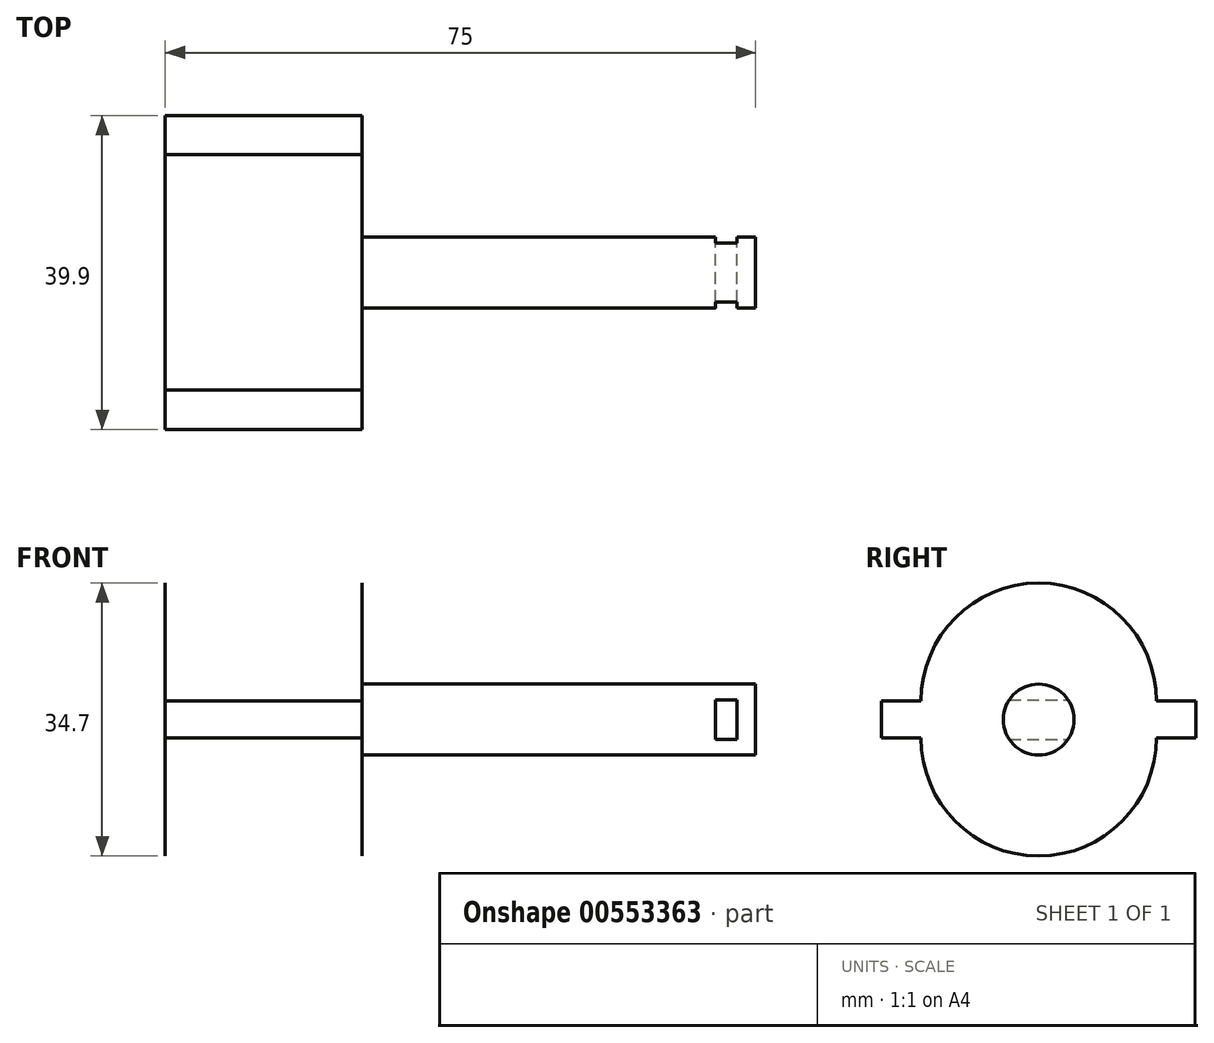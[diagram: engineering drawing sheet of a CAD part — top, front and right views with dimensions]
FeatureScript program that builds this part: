
annotation { "Feature Type Name" : "Feature", "Feature Type Description" : "" }
export const myFeature = defineFeature(function(context is Context, id is Id, definition is map)
    precondition{}
    {
        {
            var Q0;
            Q0=qCreatedBy(makeId("Right.planeOp"),FACE);
            var sketch = newSketch(context, id + "F0", { "sketchPlane" : qUnion([Q0])});
            skLineSegment(sketch, "E0.bottom", {"start": v(14.95, 17.35) * mm, "end": v(-14.95, 17.35) * mm});
            skLineSegment(sketch, "E0.top", {"start": v(14.95, -17.35) * mm, "end": v(-14.95, -17.35) * mm});
            skLineSegment(sketch, "E0.left", {"start": v(14.95, 17.35) * mm, "end": v(14.95, -17.35) * mm});
            skLineSegment(sketch, "E0.right", {"start": v(-14.95, 17.35) * mm, "end": v(-14.95, -17.35) * mm});
            skPoint(sketch, "E0.middle", {"position": v(0, 0) * mm});
            skSolve(sketch);
        }
        {
            var Q0;
            Q0=makeQuery(id+"F0.imprint","IMPRINT",FACE,{"disambiguationData":[TD([[makeQuery(id+"F0.imprint","IMPRINT",EDGE,{"derivedFrom":sQuery(id+"F0.wireOp",EDGE,"E0.bottom")}),1.0]])]});
            extrude(context, id + "F1", {"entities" : qUnion([Q0]), "oppositeDirection" : true, "depth" : 25 * mm, "offsetDistance" : 25 * mm});
        }
        {
            var Q0;
            Q0=qCreatedBy(makeId("Right.planeOp"),FACE);
            var sketch = newSketch(context, id + "F2", { "sketchPlane" : qUnion([Q0])});
            skCircle(sketch, "E1", {"center": v(0, 0) * mm, "radius": 4.5 * mm});
            skSolve(sketch);
        }
        {
            var Q0;
            Q0=makeQuery(id+"F2.imprint","IMPRINT",FACE,{"disambiguationData":[TD([[makeQuery(id+"F2.imprint","IMPRINT",EDGE,{"derivedFrom":sQuery(id+"F2.wireOp",EDGE,"E1")}),1.0]])]});
            extrude(context, id + "F3", {"entities" : qUnion([Q0]), "operationType" : NewBodyOperationType.ADD, "depth" : 50 * mm, "offsetDistance" : 25 * mm});
        }
        {
            var Q0;
            Q0=makeQuery(id+"F1.opExtrude","SWEPT_EDGE",EDGE,{"disambiguationData":[OSD([sQuery(id+"F0.wireOp",EDGE,"E0.bottom"),sQuery(id+"F0.wireOp",EDGE,"E0.right")])]});
            var Q1;
            Q1=makeQuery(id+"F1.opExtrude","SWEPT_EDGE",EDGE,{"disambiguationData":[OSD([sQuery(id+"F0.wireOp",EDGE,"E0.top"),sQuery(id+"F0.wireOp",EDGE,"E0.left")])]});
            var Q2;
            Q2=makeQuery(id+"F1.opExtrude","SWEPT_EDGE",EDGE,{"disambiguationData":[OSD([sQuery(id+"F0.wireOp",EDGE,"E0.bottom"),sQuery(id+"F0.wireOp",EDGE,"E0.left")])]});
            var Q3;
            Q3=makeQuery(id+"F1.opExtrude","SWEPT_EDGE",EDGE,{"disambiguationData":[OSD([sQuery(id+"F0.wireOp",EDGE,"E0.top"),sQuery(id+"F0.wireOp",EDGE,"E0.right")])]});
            fillet(context, id + "F4", {"entities" : qUnion([Q0, Q1, Q2, Q3]), "radius" : 15 * mm, "tangentPropagation" : true, "allowEdgeOverflow" : false});
        }
        {
            var Q0;
            Q0=makeQuery(id+"F1.opExtrude","SWEPT_FACE",FACE,{"disambiguationData":[OSD([sQuery(id+"F0.wireOp",EDGE,"E0.left")])]});
            extrude(context, id + "F5", {"entities" : qUnion([Q0]), "operationType" : NewBodyOperationType.ADD, "depth" : 5 * mm, "offsetDistance" : 25 * mm});
        }
        {
            var Q0;
            Q0=makeQuery(id+"F1.opExtrude","SWEPT_FACE",FACE,{"disambiguationData":[OSD([sQuery(id+"F0.wireOp",EDGE,"E0.right")])]});
            extrude(context, id + "F6", {"entities" : qUnion([Q0]), "operationType" : NewBodyOperationType.ADD, "depth" : 5 * mm, "offsetDistance" : 25 * mm});
        }
        {
            var Q0;
            Q0=qCreatedBy(makeId("Top.planeOp"),FACE);
            var sketch = newSketch(context, id + "F7", { "sketchPlane" : qUnion([Q0])});
            skLineSegment(sketch, "E2", {"start": v(44.9, -8.95) * mm, "end": v(47.64, -8.95) * mm});
            skLineSegment(sketch, "E3", {"start": v(47.64, -8.95) * mm, "end": v(47.64, 6.89) * mm});
            skLineSegment(sketch, "E4", {"start": v(44.9, -8.95) * mm, "end": v(44.9, 7.19) * mm});
            skLineSegment(sketch, "E5", {"start": v(44.9, 7.19) * mm, "end": v(47.64, 6.89) * mm});
            skSolve(sketch);
        }
        {
            var Q0;
            Q0=makeQuery(id+"F7.imprint","IMPRINT",FACE,{"disambiguationData":[TD([[makeQuery(id+"F7.imprint","IMPRINT",EDGE,{"derivedFrom":sQuery(id+"F7.wireOp",EDGE,"E2")}),1.0]])]});
            extrude(context, id + "F8", {"entities" : qUnion([Q0]), "operationType" : NewBodyOperationType.REMOVE, "endBound" : BoundingType.SYMMETRIC, "oppositeDirection" : true, "depth" : 5 * mm, "offsetDistance" : 25 * mm});
        }
    });
